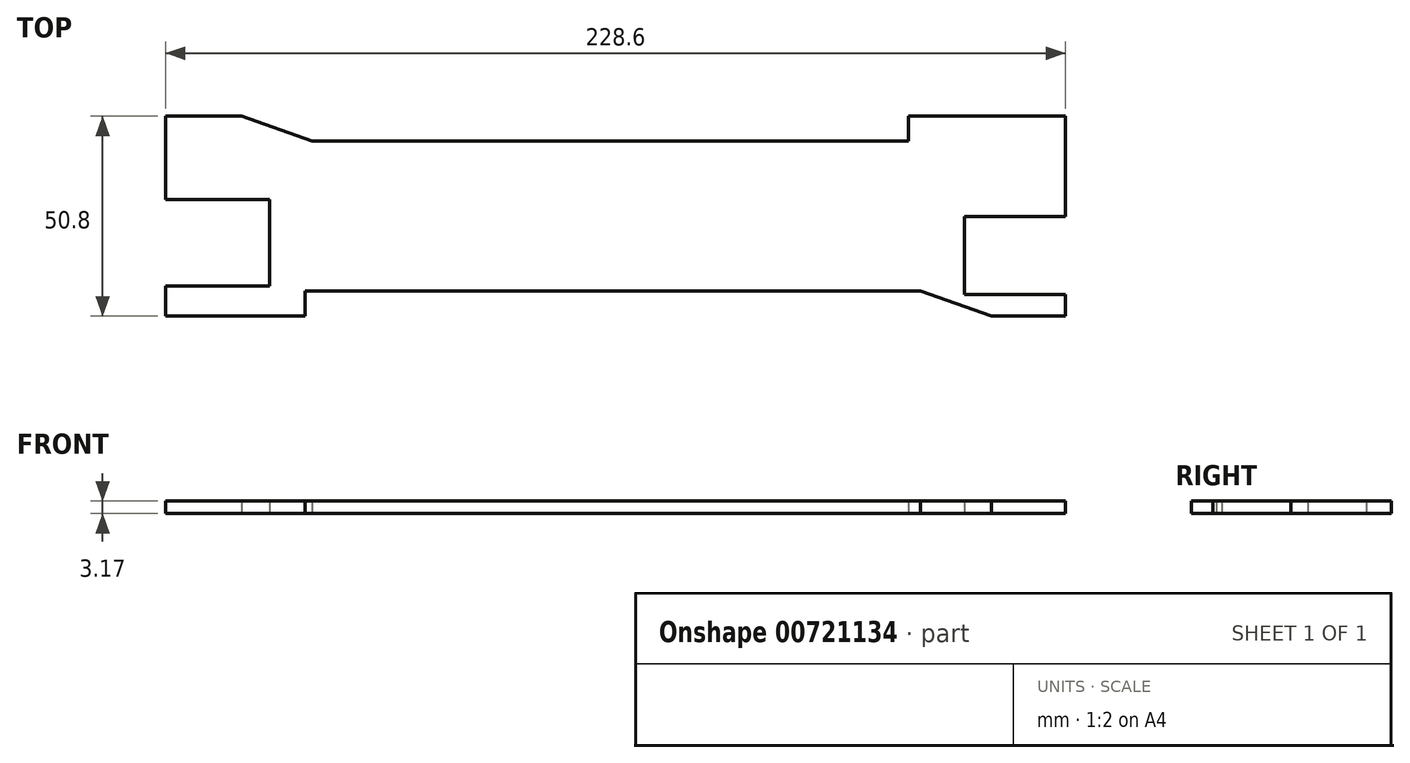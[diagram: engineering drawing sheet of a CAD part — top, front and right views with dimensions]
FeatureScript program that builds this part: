
annotation { "Feature Type Name" : "Feature", "Feature Type Description" : "" }
export const myFeature = defineFeature(function(context is Context, id is Id, definition is map)
    precondition{}
    {
        {
            var Q0;
            Q0=qCreatedBy(makeId("Top.planeOp"),FACE);
            var sketch = newSketch(context, id + "F0", { "sketchPlane" : qUnion([Q0])});
            skLineSegment(sketch, "E0.bottom", {"start": v(114.3, 25.4) * mm, "end": v(88.64, 25.4) * mm});
            skLineSegment(sketch, "E0.top", {"start": v(114.3, -25.4) * mm, "end": v(95.46, -25.4) * mm});
            skLineSegment(sketch, "E0.left", {"start": v(114.3, 25.4) * mm, "end": v(114.3, -0.13) * mm});
            skLineSegment(sketch, "E0.right", {"start": v(-114.3, 25.4) * mm, "end": v(-114.3, 4.2) * mm});
            skPoint(sketch, "E0.middle", {"position": v(0, 0) * mm});
            skLineSegment(sketch, "E1.bottom", {"start": v(-114.3, 4.2) * mm, "end": v(-87.91, 4.2) * mm});
            skLineSegment(sketch, "E1.top", {"start": v(-114.3, -17.72) * mm, "end": v(-87.91, -17.72) * mm});
            skLineSegment(sketch, "E1.right", {"start": v(-87.91, 4.2) * mm, "end": v(-87.91, -17.72) * mm});
            skLineSegment(sketch, "E2.trimOffspring", {"start": v(-114.3, -17.72) * mm, "end": v(-114.3, -25.4) * mm});
            skLineSegment(sketch, "E3.bottom", {"start": v(114.3, -0.13) * mm, "end": v(88.64, -0.13) * mm});
            skLineSegment(sketch, "E3.top", {"start": v(114.3, -19.88) * mm, "end": v(88.64, -19.88) * mm});
            skLineSegment(sketch, "E3.right", {"start": v(88.64, -0.13) * mm, "end": v(88.64, -19.88) * mm});
            skLineSegment(sketch, "E4.trimOffspring", {"start": v(114.3, -19.88) * mm, "end": v(114.3, -25.4) * mm});
            skLineSegment(sketch, "E5.top", {"start": v(77.5, -19.05) * mm, "end": v(-78.85, -19.05) * mm});
            skLineSegment(sketch, "E5.right", {"start": v(-78.85, -25.4) * mm, "end": v(-78.85, -19.05) * mm});
            skLineSegment(sketch, "E6.trimOffspring", {"start": v(-78.85, -25.4) * mm, "end": v(-114.3, -25.4) * mm});
            skPoint(sketch, "E7.oppositeSnap0", {"position": v(-87.91, -6.75) * mm});
            skLineSegment(sketch, "E8.trimOffspring", {"start": v(-95.05, 25.4) * mm, "end": v(-114.3, 25.4) * mm});
            skLineSegment(sketch, "E9", {"start": v(88.64, 25.4) * mm, "end": v(74.44, 25.4) * mm});
            skLineSegment(sketch, "E10.top", {"start": v(74.44, 19.05) * mm, "end": v(-77.1, 19.05) * mm});
            skLineSegment(sketch, "E10.left", {"start": v(74.44, 25.4) * mm, "end": v(74.44, 19.05) * mm});
            skLineSegment(sketch, "E11", {"start": v(77.5, -19.05) * mm, "end": v(95.46, -25.4) * mm});
            skLineSegment(sketch, "E12", {"start": v(-77.1, 19.05) * mm, "end": v(-95.05, 25.4) * mm});
            skSolve(sketch);
        }
        {
            var Q0;
            Q0=qSketchRegion(id+"F0",true);
            extrude(context, id + "F1", {"entities" : qUnion([Q0]), "depth" : 3.17 * mm, "offsetDistance" : 25.4 * mm});
        }
    });
